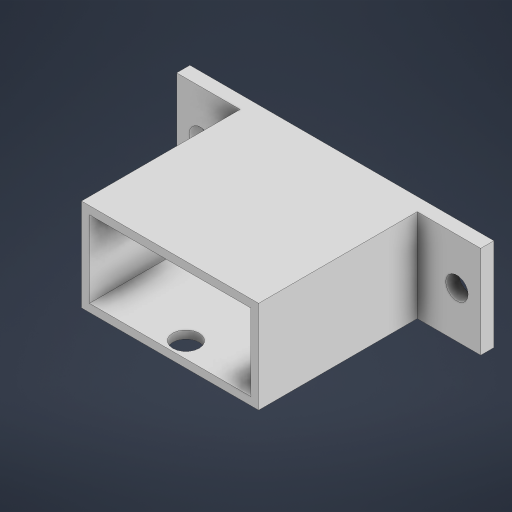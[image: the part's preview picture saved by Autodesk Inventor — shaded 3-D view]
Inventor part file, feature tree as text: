
AUTODESK INVENTOR PART (.ipt)
format: ipt  version: 2023 (Build 270158000, 158)  size: 219,648 bytes
history: native  units: mm
features: sketch x5, extrude x4, shell x1
ambient origin geometry x8: Origin, YZ Plane, XZ Plane, XY Plane, X Axis, Y Axis, Z Axis, Center Point
bodies: Solid1 (feature_tree)
feature tree (10):
  extrude  "Extrusion1"  Depth=35.0mm
  extrude  "Extrusion2"  Depth=67.0mm
  shell  "Shell1"  Thickness=60.0mm
  extrude  "Extrusion3"  Depth=10.0mm
  sketch  "Sketch4"  dims[d15=10.0mm d16=10.0mm]
  extrude  "Extrusion4"  Depth=10.0mm
  sketch  "Sketch1"  dims[d0=115.0mm d1=35.0mm]
  sketch  "Sketch2"  dims[d8=5.0mm d9=0.0mm d10=67.0mm d11=60.0mm d12=0.0mm]
  sketch  "Sketch3"  dims[d13=3.0mm d14=10.0mm]
  sketch  "Sketch5"  dims[d17=21.0mm d18=21.0mm d19=8.5mm d20=8.5mm d21=97.0mm d22=9.0mm d23=9.0mm d24=0.0mm d25=0.0mm d26=10.0mm d27=6.0mm d28=3.0mm d29=0.0mm d30=0.25mm d31=0.375mm d32=14.3117mm d33=0.75mm d34=20.594885mm d35=0.0625mm d36=0.75mm d37=0.375mm]
